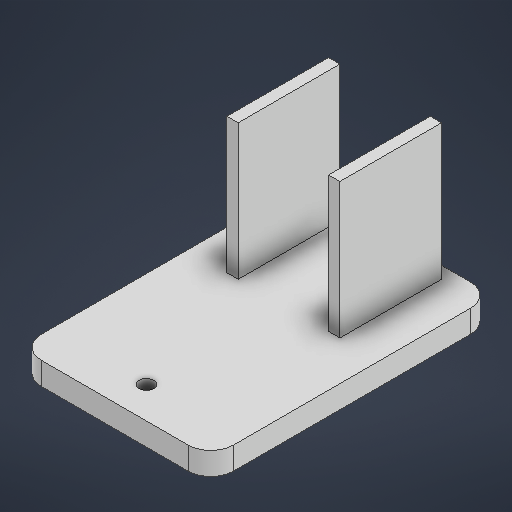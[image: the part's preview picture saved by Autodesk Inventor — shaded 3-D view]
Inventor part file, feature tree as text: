
AUTODESK INVENTOR PART (.ipt)
format: ipt  version: 2025 (Build 290162000, 162)  size: 285,696 bytes
history: native  units: in
note: dims shown in document units (in); Inventor stores cm internally (conversion verified against a paired STEP export)
features: extrude x4, sketch x4
ambient origin geometry x8: Origin, YZ Plane, XZ Plane, XY Plane, X Axis, Y Axis, Z Axis, Center Point
bodies: Body1 (feature_tree)
feature tree (8):
  extrude  "Extrusion6"  Depth=3.3465in
  extrude  "Extrusion7"  Depth=4.9213in
  extrude  "Extrusion8"  Depth=3.3465in
  extrude  "Extrusion9"  Depth=0.4331in
  sketch  "Sketch6"  dims[d26=0.0787in d31=0.0787in d42=3.3465in]
  sketch  "Sketch7"  dims[d43=4.9213in d44=0.2559in]
  sketch  "Sketch8"  dims[d45=0.2559in d46=3.3465in]
  sketch  "Sketch9"  dims[d47=0.3937in d48=0.4331in d49=0.4331in d50=0.0787in d51=0.0in d52=0.4331in d53=0.4331in d54=4.9213in d55=0.123in d56=0.0in d57=0.1919in d58=0.0in d61=0.3937in d62=0.3937in d65=0.1969in d66=1.7717in d67=0.7874in d68=2.3622in d69=0.0in d18=0.0197in d19=0.0344in d20=0.0197in d21=0.0344in]
